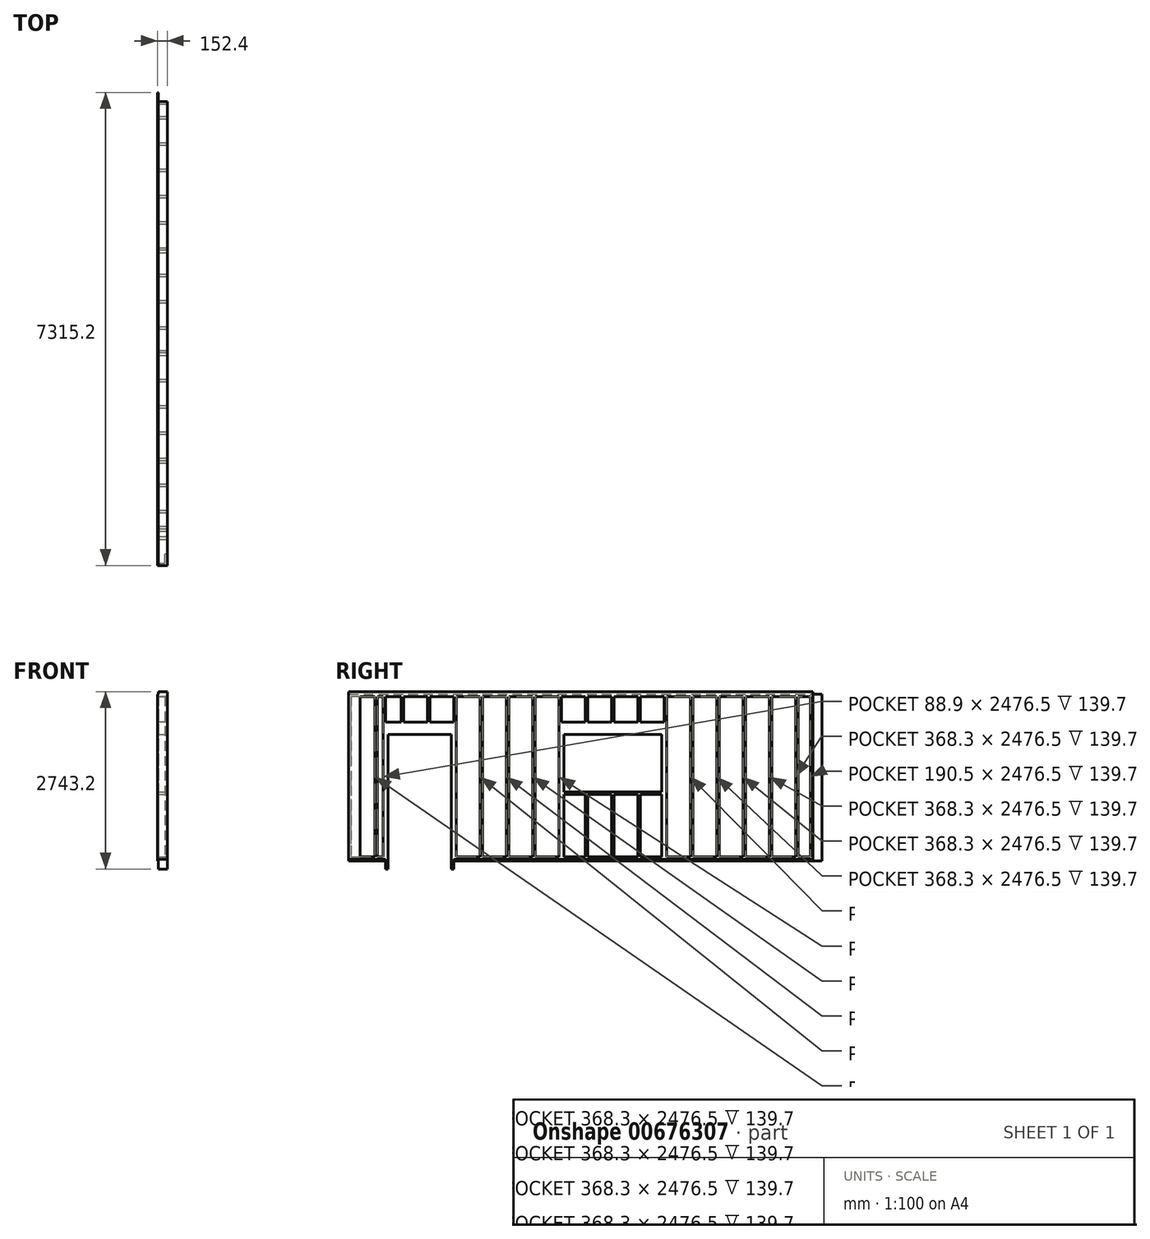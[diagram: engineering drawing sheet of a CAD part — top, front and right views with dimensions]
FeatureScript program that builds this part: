
annotation { "Feature Type Name" : "Feature", "Feature Type Description" : "" }
export const myFeature = defineFeature(function(context is Context, id is Id, definition is map)
    precondition{}
    {
        {
            var Q0;
            Q0=qCreatedBy(makeId("Top.planeOp"),FACE);
            var sketch = newSketch(context, id + "F0", { "sketchPlane" : qUnion([Q0])});
            skLineSegment(sketch, "E0.bottom", {"start": v(-69.85, 3587.75) * mm, "end": v(69.85, 3587.75) * mm});
            skLineSegment(sketch, "E0.top", {"start": v(-69.85, -3587.75) * mm, "end": v(69.85, -3587.75) * mm});
            skLineSegment(sketch, "E0.left", {"start": v(-69.85, 3587.75) * mm, "end": v(-69.85, -3587.75) * mm});
            skLineSegment(sketch, "E0.right", {"start": v(69.85, 3587.75) * mm, "end": v(69.85, -3587.75) * mm});
            skPoint(sketch, "E0.middle", {"position": v(0, 0) * mm});
            skSolve(sketch);
        }
        {
            var Q0;
            Q0 = qSketchRegion(id + "F0", true);
            extrude(context, id + "F1", {"entities" : qUnion([Q0]), "depth" : 38.1 * mm, "offsetDistance" : 25.4 * mm});
        }
        {
            var Q0;
            Q0=makeQuery(id+"F1.opExtrude","SWEPT_FACE",FACE,{"disambiguationData":[OSD([sQuery(id+"F0.wireOp",EDGE,"E0.right")])]});
            var sketch = newSketch(context, id + "F2", { "sketchPlane" : qUnion([Q0])});
            skLineSegment(sketch, "E1.bottom", {"start": v(-3587.75, 38.1) * mm, "end": v(3587.75, 38.1) * mm, "construction": true});
            skLineSegment(sketch, "E1.top", {"start": v(-3587.75, 2590.8) * mm, "end": v(3587.75, 2590.8) * mm});
            skLineSegment(sketch, "E1.left", {"start": v(-3587.75, 38.1) * mm, "end": v(-3587.75, 2590.8) * mm});
            skLineSegment(sketch, "E1.right", {"start": v(3587.75, 38.1) * mm, "end": v(3587.75, 2590.8) * mm});
            skLineSegment(sketch, "E2.0", {"start": v(3549.65, 38.1) * mm, "end": v(3549.65, 2514.6) * mm});
            skLineSegment(sketch, "E3.0", {"start": v(-3549.65, 38.1) * mm, "end": v(-3549.65, 2514.6) * mm});
            skLineSegment(sketch, "E4", {"start": v(3549.65, 38.1) * mm, "end": v(3587.75, 38.1) * mm});
            skLineSegment(sketch, "E5", {"start": v(-3549.65, 38.1) * mm, "end": v(-3587.75, 38.1) * mm});
            skLineSegment(sketch, "E6.trimOffspring", {"start": v(-3549.65, 2514.6) * mm, "end": v(3549.65, 2514.6) * mm});
            skSolve(sketch);
        }
        {
            var Q0;
            Q0 = qSketchRegion(id + "F2", true);
            var Q1;
            Q1=makeQuery(id+"F1.opExtrude","SWEPT_FACE",FACE,{"disambiguationData":[OSD([sQuery(id+"F0.wireOp",EDGE,"E0.left")])]});
            extrude(context, id + "F3", {"entities" : qUnion([Q0]), "operationType" : NewBodyOperationType.ADD, "endBound" : BoundingType.UP_TO_SURFACE, "oppositeDirection" : true, "depth" : 289.56 * mm, "endBoundEntityFace" : qUnion([Q1]), "offsetDistance" : 25.4 * mm});
        }
        {
            var Q0;
            Q0=makeQuery(id+"F1.opExtrude","CAP_FACE",FACE,{"disambiguationData":[OSD([sQuery(id+"F0.wireOp",EDGE,"E0.bottom"),sQuery(id+"F0.wireOp",EDGE,"E0.top"),sQuery(id+"F0.wireOp",EDGE,"E0.left"),sQuery(id+"F0.wireOp",EDGE,"E0.right")])],"isStart":false});
            var sketch = newSketch(context, id + "F4", { "sketchPlane" : qUnion([Q0])});
            skLineSegment(sketch, "E7.bottom", {"start": v(-69.85, -3181.35) * mm, "end": v(69.85, -3181.35) * mm});
            skLineSegment(sketch, "E7.top", {"start": v(-69.85, -3143.25) * mm, "end": v(69.85, -3143.25) * mm});
            skLineSegment(sketch, "E7.left", {"start": v(-69.85, -3181.35) * mm, "end": v(-69.85, -3143.25) * mm});
            skLineSegment(sketch, "E7.right", {"start": v(69.85, -3181.35) * mm, "end": v(69.85, -3143.25) * mm});
            skLineSegment(sketch, "E8.0.1.0", {"start": v(69.85, -2774.95) * mm, "end": v(69.85, -2736.85) * mm});
            skLineSegment(sketch, "E8.0.1.1", {"start": v(-69.85, -2736.85) * mm, "end": v(69.85, -2736.85) * mm});
            skLineSegment(sketch, "E8.0.1.2", {"start": v(-69.85, -2774.95) * mm, "end": v(69.85, -2774.95) * mm});
            skLineSegment(sketch, "E8.0.1.3", {"start": v(-69.85, -2774.95) * mm, "end": v(-69.85, -2736.85) * mm});
            skLineSegment(sketch, "E8.0.2.0", {"start": v(69.85, -2368.55) * mm, "end": v(69.85, -2330.45) * mm});
            skLineSegment(sketch, "E8.0.2.1", {"start": v(-69.85, -2330.45) * mm, "end": v(69.85, -2330.45) * mm});
            skLineSegment(sketch, "E8.0.2.2", {"start": v(-69.85, -2368.55) * mm, "end": v(69.85, -2368.55) * mm});
            skLineSegment(sketch, "E8.0.2.3", {"start": v(-69.85, -2368.55) * mm, "end": v(-69.85, -2330.45) * mm});
            skLineSegment(sketch, "E8.0.3.0", {"start": v(69.85, -1962.15) * mm, "end": v(69.85, -1924.05) * mm});
            skLineSegment(sketch, "E8.0.3.1", {"start": v(-69.85, -1924.05) * mm, "end": v(69.85, -1924.05) * mm});
            skLineSegment(sketch, "E8.0.3.2", {"start": v(-69.85, -1962.15) * mm, "end": v(69.85, -1962.15) * mm});
            skLineSegment(sketch, "E8.0.3.3", {"start": v(-69.85, -1962.15) * mm, "end": v(-69.85, -1924.05) * mm});
            skLineSegment(sketch, "E8.0.4.0", {"start": v(69.85, -1555.75) * mm, "end": v(69.85, -1517.65) * mm});
            skLineSegment(sketch, "E8.0.4.1", {"start": v(-69.85, -1517.65) * mm, "end": v(69.85, -1517.65) * mm});
            skLineSegment(sketch, "E8.0.4.2", {"start": v(-69.85, -1555.75) * mm, "end": v(69.85, -1555.75) * mm});
            skLineSegment(sketch, "E8.0.4.3", {"start": v(-69.85, -1555.75) * mm, "end": v(-69.85, -1517.65) * mm});
            skLineSegment(sketch, "E8.0.5.0", {"start": v(69.85, -1149.35) * mm, "end": v(69.85, -1111.25) * mm});
            skLineSegment(sketch, "E8.0.5.1", {"start": v(-69.85, -1111.25) * mm, "end": v(69.85, -1111.25) * mm});
            skLineSegment(sketch, "E8.0.5.2", {"start": v(-69.85, -1149.35) * mm, "end": v(69.85, -1149.35) * mm});
            skLineSegment(sketch, "E8.0.5.3", {"start": v(-69.85, -1149.35) * mm, "end": v(-69.85, -1111.25) * mm});
            skLineSegment(sketch, "E8.0.6.0", {"start": v(69.85, -742.95) * mm, "end": v(69.85, -704.85) * mm});
            skLineSegment(sketch, "E8.0.6.1", {"start": v(-69.85, -704.85) * mm, "end": v(69.85, -704.85) * mm});
            skLineSegment(sketch, "E8.0.6.2", {"start": v(-69.85, -742.95) * mm, "end": v(69.85, -742.95) * mm});
            skLineSegment(sketch, "E8.0.6.3", {"start": v(-69.85, -742.95) * mm, "end": v(-69.85, -704.85) * mm});
            skLineSegment(sketch, "E8.0.7.0", {"start": v(69.85, -336.55) * mm, "end": v(69.85, -298.45) * mm});
            skLineSegment(sketch, "E8.0.7.1", {"start": v(-69.85, -298.45) * mm, "end": v(69.85, -298.45) * mm});
            skLineSegment(sketch, "E8.0.7.2", {"start": v(-69.85, -336.55) * mm, "end": v(69.85, -336.55) * mm});
            skLineSegment(sketch, "E8.0.7.3", {"start": v(-69.85, -336.55) * mm, "end": v(-69.85, -298.45) * mm});
            skLineSegment(sketch, "E8.0.8.0", {"start": v(69.85, 69.85) * mm, "end": v(69.85, 107.95) * mm});
            skLineSegment(sketch, "E8.0.8.1", {"start": v(-69.85, 107.95) * mm, "end": v(69.85, 107.95) * mm});
            skLineSegment(sketch, "E8.0.8.2", {"start": v(-69.85, 69.85) * mm, "end": v(69.85, 69.85) * mm});
            skLineSegment(sketch, "E8.0.8.3", {"start": v(-69.85, 69.85) * mm, "end": v(-69.85, 107.95) * mm});
            skLineSegment(sketch, "E8.0.9.0", {"start": v(69.85, 476.25) * mm, "end": v(69.85, 514.35) * mm});
            skLineSegment(sketch, "E8.0.9.1", {"start": v(-69.85, 514.35) * mm, "end": v(69.85, 514.35) * mm});
            skLineSegment(sketch, "E8.0.9.2", {"start": v(-69.85, 476.25) * mm, "end": v(69.85, 476.25) * mm});
            skLineSegment(sketch, "E8.0.9.3", {"start": v(-69.85, 476.25) * mm, "end": v(-69.85, 514.35) * mm});
            skLineSegment(sketch, "E8.0.10.0", {"start": v(69.85, 882.65) * mm, "end": v(69.85, 920.75) * mm});
            skLineSegment(sketch, "E8.0.10.1", {"start": v(-69.85, 920.75) * mm, "end": v(69.85, 920.75) * mm});
            skLineSegment(sketch, "E8.0.10.2", {"start": v(-69.85, 882.65) * mm, "end": v(69.85, 882.65) * mm});
            skLineSegment(sketch, "E8.0.10.3", {"start": v(-69.85, 882.65) * mm, "end": v(-69.85, 920.75) * mm});
            skLineSegment(sketch, "E8.0.11.0", {"start": v(69.85, 1289.05) * mm, "end": v(69.85, 1327.15) * mm});
            skLineSegment(sketch, "E8.0.11.1", {"start": v(-69.85, 1327.15) * mm, "end": v(69.85, 1327.15) * mm});
            skLineSegment(sketch, "E8.0.11.2", {"start": v(-69.85, 1289.05) * mm, "end": v(69.85, 1289.05) * mm});
            skLineSegment(sketch, "E8.0.11.3", {"start": v(-69.85, 1289.05) * mm, "end": v(-69.85, 1327.15) * mm});
            skLineSegment(sketch, "E8.0.12.0", {"start": v(69.85, 1695.45) * mm, "end": v(69.85, 1733.55) * mm});
            skLineSegment(sketch, "E8.0.12.1", {"start": v(-69.85, 1733.55) * mm, "end": v(69.85, 1733.55) * mm});
            skLineSegment(sketch, "E8.0.12.2", {"start": v(-69.85, 1695.45) * mm, "end": v(69.85, 1695.45) * mm});
            skLineSegment(sketch, "E8.0.12.3", {"start": v(-69.85, 1695.45) * mm, "end": v(-69.85, 1733.55) * mm});
            skLineSegment(sketch, "E8.0.13.0", {"start": v(69.85, 2101.85) * mm, "end": v(69.85, 2139.95) * mm});
            skLineSegment(sketch, "E8.0.13.1", {"start": v(-69.85, 2139.95) * mm, "end": v(69.85, 2139.95) * mm});
            skLineSegment(sketch, "E8.0.13.2", {"start": v(-69.85, 2101.85) * mm, "end": v(69.85, 2101.85) * mm});
            skLineSegment(sketch, "E8.0.13.3", {"start": v(-69.85, 2101.85) * mm, "end": v(-69.85, 2139.95) * mm});
            skLineSegment(sketch, "E8.0.14.0", {"start": v(69.85, 2508.25) * mm, "end": v(69.85, 2546.35) * mm});
            skLineSegment(sketch, "E8.0.14.1", {"start": v(-69.85, 2546.35) * mm, "end": v(69.85, 2546.35) * mm});
            skLineSegment(sketch, "E8.0.14.2", {"start": v(-69.85, 2508.25) * mm, "end": v(69.85, 2508.25) * mm});
            skLineSegment(sketch, "E8.0.14.3", {"start": v(-69.85, 2508.25) * mm, "end": v(-69.85, 2546.35) * mm});
            skLineSegment(sketch, "E8.0.15.0", {"start": v(69.85, 2914.65) * mm, "end": v(69.85, 2952.75) * mm});
            skLineSegment(sketch, "E8.0.15.1", {"start": v(-69.85, 2952.75) * mm, "end": v(69.85, 2952.75) * mm});
            skLineSegment(sketch, "E8.0.15.2", {"start": v(-69.85, 2914.65) * mm, "end": v(69.85, 2914.65) * mm});
            skLineSegment(sketch, "E8.0.15.3", {"start": v(-69.85, 2914.65) * mm, "end": v(-69.85, 2952.75) * mm});
            skLineSegment(sketch, "E8.0.16.0", {"start": v(69.85, 3321.05) * mm, "end": v(69.85, 3359.15) * mm});
            skLineSegment(sketch, "E8.0.16.1", {"start": v(-69.85, 3359.15) * mm, "end": v(69.85, 3359.15) * mm});
            skLineSegment(sketch, "E8.0.16.2", {"start": v(-69.85, 3321.05) * mm, "end": v(69.85, 3321.05) * mm});
            skLineSegment(sketch, "E8.0.16.3", {"start": v(-69.85, 3321.05) * mm, "end": v(-69.85, 3359.15) * mm});
            skLineSegment(sketch, "E8.direction1", {"start": v(-69.85, -3181.35) * mm, "end": v(-44.45, -3181.35) * mm, "construction": true});
            skLineSegment(sketch, "E8.direction2", {"start": v(-69.85, -3181.35) * mm, "end": v(-69.85, -2774.95) * mm, "construction": true});
            skLineSegment(sketch, "E9.bottom", {"start": v(69.85, -3549.65) * mm, "end": v(31.75, -3549.65) * mm});
            skLineSegment(sketch, "E9.top", {"start": v(69.85, -3409.95) * mm, "end": v(31.75, -3409.95) * mm});
            skLineSegment(sketch, "E9.left", {"start": v(69.85, -3549.65) * mm, "end": v(69.85, -3409.95) * mm});
            skLineSegment(sketch, "E9.right", {"start": v(31.75, -3549.65) * mm, "end": v(31.75, -3409.95) * mm});
            skSolve(sketch);
        }
        {
            var Q0;
            Q0 = qSketchRegion(id + "F4", true);
            var Q1;
            Q1=makeQuery(id+"F3.opExtrude","SWEPT_FACE",FACE,{"disambiguationData":[OSD([sQuery(id+"F2.wireOp",EDGE,"E6.trimOffspring")])]});
            extrude(context, id + "F5", {"entities" : qUnion([Q0]), "operationType" : NewBodyOperationType.ADD, "endBound" : BoundingType.UP_TO_SURFACE, "depth" : 25.4 * mm, "endBoundEntityFace" : qUnion([Q1]), "offsetDistance" : 25.4 * mm});
        }
        {
            var Q0;
            Q0=makeQuery(id+"F5.boolean.opBoolean","MERGE",FACE,{"derivedFrom":[makeQuery(id+"F3.boolean.opBoolean","MERGE",FACE,{"derivedFrom":[makeQuery(id+"F1.opExtrude","SWEPT_FACE",FACE,{"disambiguationData":[OSD([sQuery(id+"F0.wireOp",EDGE,"E0.right")])]}),makeQuery(id+"F3.opExtrude","CAP_FACE",FACE,{"disambiguationData":[OSD([sQuery(id+"F2.wireOp",EDGE,"E1.top"),sQuery(id+"F2.wireOp",EDGE,"E1.left"),sQuery(id+"F2.wireOp",EDGE,"E1.right"),sQuery(id+"F2.wireOp",EDGE,"E2.0"),sQuery(id+"F2.wireOp",EDGE,"E3.0"),sQuery(id+"F2.wireOp",EDGE,"E4"),sQuery(id+"F2.wireOp",EDGE,"E5"),sQuery(id+"F2.wireOp",EDGE,"E6.trimOffspring")])],"isStart":true})]}),makeQuery(id+"F5.opExtrude","SWEPT_FACE",FACE,{"disambiguationData":[OSD([sQuery(id+"F4.wireOp",EDGE,"E7.right")])]}),makeQuery(id+"F5.opExtrude","SWEPT_FACE",FACE,{"disambiguationData":[OSD([sQuery(id+"F4.wireOp",EDGE,"E8.0.1.0")])]}),makeQuery(id+"F5.opExtrude","SWEPT_FACE",FACE,{"disambiguationData":[OSD([sQuery(id+"F4.wireOp",EDGE,"E8.0.2.0")])]}),makeQuery(id+"F5.opExtrude","SWEPT_FACE",FACE,{"disambiguationData":[OSD([sQuery(id+"F4.wireOp",EDGE,"E8.0.3.0")])]}),makeQuery(id+"F5.opExtrude","SWEPT_FACE",FACE,{"disambiguationData":[OSD([sQuery(id+"F4.wireOp",EDGE,"E8.0.4.0")])]}),makeQuery(id+"F5.opExtrude","SWEPT_FACE",FACE,{"disambiguationData":[OSD([sQuery(id+"F4.wireOp",EDGE,"E8.0.5.0")])]}),makeQuery(id+"F5.opExtrude","SWEPT_FACE",FACE,{"disambiguationData":[OSD([sQuery(id+"F4.wireOp",EDGE,"E8.0.6.0")])]}),makeQuery(id+"F5.opExtrude","SWEPT_FACE",FACE,{"disambiguationData":[OSD([sQuery(id+"F4.wireOp",EDGE,"E8.0.7.0")])]}),makeQuery(id+"F5.opExtrude","SWEPT_FACE",FACE,{"disambiguationData":[OSD([sQuery(id+"F4.wireOp",EDGE,"E8.0.8.0")])]}),makeQuery(id+"F5.opExtrude","SWEPT_FACE",FACE,{"disambiguationData":[OSD([sQuery(id+"F4.wireOp",EDGE,"E8.0.9.0")])]}),makeQuery(id+"F5.opExtrude","SWEPT_FACE",FACE,{"disambiguationData":[OSD([sQuery(id+"F4.wireOp",EDGE,"E8.0.10.0")])]}),makeQuery(id+"F5.opExtrude","SWEPT_FACE",FACE,{"disambiguationData":[OSD([sQuery(id+"F4.wireOp",EDGE,"E8.0.11.0")])]}),makeQuery(id+"F5.opExtrude","SWEPT_FACE",FACE,{"disambiguationData":[OSD([sQuery(id+"F4.wireOp",EDGE,"E8.0.12.0")])]}),makeQuery(id+"F5.opExtrude","SWEPT_FACE",FACE,{"disambiguationData":[OSD([sQuery(id+"F4.wireOp",EDGE,"E8.0.13.0")])]}),makeQuery(id+"F5.opExtrude","SWEPT_FACE",FACE,{"disambiguationData":[OSD([sQuery(id+"F4.wireOp",EDGE,"E8.0.14.0")])]}),makeQuery(id+"F5.opExtrude","SWEPT_FACE",FACE,{"disambiguationData":[OSD([sQuery(id+"F4.wireOp",EDGE,"E8.0.15.0")])]}),makeQuery(id+"F5.opExtrude","SWEPT_FACE",FACE,{"disambiguationData":[OSD([sQuery(id+"F4.wireOp",EDGE,"E8.0.16.0")])]})]});
            var sketch = newSketch(context, id + "F6", { "sketchPlane" : qUnion([Q0])});
            skLineSegment(sketch, "E10", {"start": v(-3054.35, 38.1) * mm, "end": v(-3054.35, 2514.6) * mm});
            skLineSegment(sketch, "E11", {"start": v(-3054.35, 2514.6) * mm, "end": v(-3016.25, 2514.6) * mm});
            skLineSegment(sketch, "E12", {"start": v(-3016.25, 2514.6) * mm, "end": v(-3016.25, 2120.9) * mm});
            skLineSegment(sketch, "E13", {"start": v(-3016.25, 2120.9) * mm, "end": v(-1962.15, 2120.9) * mm});
            skLineSegment(sketch, "E14", {"start": v(-2000.25, 38.1) * mm, "end": v(-2000.25, 1930.4) * mm});
            skLineSegment(sketch, "E15", {"start": v(-2000.25, 1930.4) * mm, "end": v(-2978.15, 1930.4) * mm});
            skLineSegment(sketch, "E16", {"start": v(-2978.15, 1930.4) * mm, "end": v(-2978.15, 38.1) * mm});
            skLineSegment(sketch, "E17", {"start": v(-2978.15, 38.1) * mm, "end": v(-3054.35, 38.1) * mm});
            skLineSegment(sketch, "E18", {"start": v(-1962.15, 2120.9) * mm, "end": v(-1962.15, 38.1) * mm});
            skLineSegment(sketch, "E19", {"start": v(-1962.15, 38.1) * mm, "end": v(-2000.25, 38.1) * mm});
            skLineSegment(sketch, "E20.bottom", {"start": v(-260.35, 1930.4) * mm, "end": v(1250.95, 1930.4) * mm});
            skLineSegment(sketch, "E20.top", {"start": v(-260.35, 1041.4) * mm, "end": v(1250.95, 1041.4) * mm});
            skLineSegment(sketch, "E20.left", {"start": v(-260.35, 1930.4) * mm, "end": v(-260.35, 1041.4) * mm});
            skLineSegment(sketch, "E20.right", {"start": v(1250.95, 1930.4) * mm, "end": v(1250.95, 1041.4) * mm});
            skLineSegment(sketch, "E21", {"start": v(-260.35, 1003.3) * mm, "end": v(-260.35, 38.1) * mm});
            skLineSegment(sketch, "E22", {"start": v(-260.35, 38.1) * mm, "end": v(-298.45, 38.1) * mm});
            skLineSegment(sketch, "E23", {"start": v(-298.45, 38.1) * mm, "end": v(-298.45, 2120.9) * mm});
            skLineSegment(sketch, "E24", {"start": v(-298.45, 2120.9) * mm, "end": v(1289.05, 2120.9) * mm});
            skLineSegment(sketch, "E25", {"start": v(1289.05, 2120.9) * mm, "end": v(1289.05, 38.1) * mm});
            skLineSegment(sketch, "E26", {"start": v(1289.05, 38.1) * mm, "end": v(1250.95, 38.1) * mm});
            skLineSegment(sketch, "E27", {"start": v(1250.95, 38.1) * mm, "end": v(1250.95, 1003.3) * mm});
            skLineSegment(sketch, "E28", {"start": v(1250.95, 1003.3) * mm, "end": v(-260.35, 1003.3) * mm});
            skLineSegment(sketch, "E29.bottom", {"start": v(-3016.25, 0) * mm, "end": v(-2978.15, 0) * mm});
            skLineSegment(sketch, "E29.top", {"start": v(-3016.25, -152.4) * mm, "end": v(-2978.15, -152.4) * mm});
            skLineSegment(sketch, "E29.left", {"start": v(-3016.25, 0) * mm, "end": v(-3016.25, -152.4) * mm});
            skLineSegment(sketch, "E29.right", {"start": v(-2978.15, 0) * mm, "end": v(-2978.15, -152.4) * mm});
            skLineSegment(sketch, "E30.bottom", {"start": v(-1962.15, 0) * mm, "end": v(-2000.25, 0) * mm});
            skLineSegment(sketch, "E30.top", {"start": v(-1962.15, -152.4) * mm, "end": v(-2000.25, -152.4) * mm});
            skLineSegment(sketch, "E30.left", {"start": v(-1962.15, 0) * mm, "end": v(-1962.15, -152.4) * mm});
            skLineSegment(sketch, "E30.right", {"start": v(-2000.25, 0) * mm, "end": v(-2000.25, -152.4) * mm});
            skSolve(sketch);
        }
        {
            var Q0;
            Q0 = qSketchRegion(id + "F6", true);
            extrude(context, id + "F7", {"entities" : qUnion([Q0]), "operationType" : NewBodyOperationType.ADD, "oppositeDirection" : true, "depth" : 139.7 * mm, "offsetDistance" : 25.4 * mm});
        }
        {
            var Q0;
            {var subQ0=sQuery(id+"F0.wireOp",EDGE,"E0.left");Q0=makeQuery(id+"F7.boolean.opBoolean","MERGE",FACE,{"derivedFrom":[makeQuery(id+"F5.boolean.opBoolean","MERGE",FACE,{"derivedFrom":[makeQuery(id+"F3.boolean.opBoolean","MERGE",FACE,{"derivedFrom":[makeQuery(id+"F1.opExtrude","SWEPT_FACE",FACE,{"disambiguationData":[OSD([subQ0])]}),makeQuery(id+"F3.opExtrude","CAP_FACE",FACE,{"disambiguationData":[OSD([subQ0])],"isStart":false})]}),makeQuery(id+"F5.opExtrude","SWEPT_FACE",FACE,{"disambiguationData":[OSD([sQuery(id+"F4.wireOp",EDGE,"E7.left")])]}),makeQuery(id+"F5.opExtrude","SWEPT_FACE",FACE,{"disambiguationData":[OSD([sQuery(id+"F4.wireOp",EDGE,"E8.0.1.3")])]}),makeQuery(id+"F5.opExtrude","SWEPT_FACE",FACE,{"disambiguationData":[OSD([sQuery(id+"F4.wireOp",EDGE,"E8.0.2.3")])]}),makeQuery(id+"F5.opExtrude","SWEPT_FACE",FACE,{"disambiguationData":[OSD([sQuery(id+"F4.wireOp",EDGE,"E8.0.3.3")])]}),makeQuery(id+"F5.opExtrude","SWEPT_FACE",FACE,{"disambiguationData":[OSD([sQuery(id+"F4.wireOp",EDGE,"E8.0.4.3")])]}),makeQuery(id+"F5.opExtrude","SWEPT_FACE",FACE,{"disambiguationData":[OSD([sQuery(id+"F4.wireOp",EDGE,"E8.0.5.3")])]}),makeQuery(id+"F5.opExtrude","SWEPT_FACE",FACE,{"disambiguationData":[OSD([sQuery(id+"F4.wireOp",EDGE,"E8.0.6.3")])]}),makeQuery(id+"F5.opExtrude","SWEPT_FACE",FACE,{"disambiguationData":[OSD([sQuery(id+"F4.wireOp",EDGE,"E8.0.7.3")])]}),makeQuery(id+"F5.opExtrude","SWEPT_FACE",FACE,{"disambiguationData":[OSD([sQuery(id+"F4.wireOp",EDGE,"E8.0.8.3")])]}),makeQuery(id+"F5.opExtrude","SWEPT_FACE",FACE,{"disambiguationData":[OSD([sQuery(id+"F4.wireOp",EDGE,"E8.0.9.3")])]}),makeQuery(id+"F5.opExtrude","SWEPT_FACE",FACE,{"disambiguationData":[OSD([sQuery(id+"F4.wireOp",EDGE,"E8.0.10.3")])]}),makeQuery(id+"F5.opExtrude","SWEPT_FACE",FACE,{"disambiguationData":[OSD([sQuery(id+"F4.wireOp",EDGE,"E8.0.11.3")])]}),makeQuery(id+"F5.opExtrude","SWEPT_FACE",FACE,{"disambiguationData":[OSD([sQuery(id+"F4.wireOp",EDGE,"E8.0.12.3")])]}),makeQuery(id+"F5.opExtrude","SWEPT_FACE",FACE,{"disambiguationData":[OSD([sQuery(id+"F4.wireOp",EDGE,"E8.0.13.3")])]}),makeQuery(id+"F5.opExtrude","SWEPT_FACE",FACE,{"disambiguationData":[OSD([sQuery(id+"F4.wireOp",EDGE,"E8.0.14.3")])]}),makeQuery(id+"F5.opExtrude","SWEPT_FACE",FACE,{"disambiguationData":[OSD([sQuery(id+"F4.wireOp",EDGE,"E8.0.15.3")])]}),makeQuery(id+"F5.opExtrude","SWEPT_FACE",FACE,{"disambiguationData":[OSD([sQuery(id+"F4.wireOp",EDGE,"E8.0.16.3")])]})]}),makeQuery(id+"F7.opExtrude","CAP_FACE",FACE,{"disambiguationData":[OSD([sQuery(id+"F6.wireOp",EDGE,"E10"),sQuery(id+"F6.wireOp",EDGE,"E11"),sQuery(id+"F6.wireOp",EDGE,"E12"),sQuery(id+"F6.wireOp",EDGE,"E13"),sQuery(id+"F6.wireOp",EDGE,"E14"),sQuery(id+"F6.wireOp",EDGE,"E15"),sQuery(id+"F6.wireOp",EDGE,"E16"),sQuery(id+"F6.wireOp",EDGE,"E17"),sQuery(id+"F6.wireOp",EDGE,"E18"),sQuery(id+"F6.wireOp",EDGE,"E19")])],"isStart":false}),makeQuery(id+"F7.opExtrude","CAP_FACE",FACE,{"disambiguationData":[OSD([sQuery(id+"F6.wireOp",EDGE,"E20.bottom"),sQuery(id+"F6.wireOp",EDGE,"E20.top"),sQuery(id+"F6.wireOp",EDGE,"E20.left"),sQuery(id+"F6.wireOp",EDGE,"E20.right"),sQuery(id+"F6.wireOp",EDGE,"E21"),sQuery(id+"F6.wireOp",EDGE,"E22"),sQuery(id+"F6.wireOp",EDGE,"E23"),sQuery(id+"F6.wireOp",EDGE,"E24"),sQuery(id+"F6.wireOp",EDGE,"E25"),sQuery(id+"F6.wireOp",EDGE,"E26"),sQuery(id+"F6.wireOp",EDGE,"E27"),sQuery(id+"F6.wireOp",EDGE,"E28")])],"isStart":false}),makeQuery(id+"F7.opExtrude","CAP_FACE",FACE,{"disambiguationData":[OSD([sQuery(id+"F6.wireOp",EDGE,"E29.bottom"),sQuery(id+"F6.wireOp",EDGE,"E29.top"),sQuery(id+"F6.wireOp",EDGE,"E29.left"),sQuery(id+"F6.wireOp",EDGE,"E29.right")])],"isStart":false}),makeQuery(id+"F7.opExtrude","CAP_FACE",FACE,{"disambiguationData":[OSD([sQuery(id+"F6.wireOp",EDGE,"E30.bottom"),sQuery(id+"F6.wireOp",EDGE,"E30.top"),sQuery(id+"F6.wireOp",EDGE,"E30.left"),sQuery(id+"F6.wireOp",EDGE,"E30.right")])],"isStart":false})]});}
            var sketch = newSketch(context, id + "F8", { "sketchPlane" : qUnion([Q0])});
            skLineSegment(sketch, "E31.bottom", {"start": v(3587.75, 2552.7) * mm, "end": v(-3727.45, 2552.7) * mm});
            skLineSegment(sketch, "E31.top", {"start": v(3587.75, -25.4) * mm, "end": v(-3727.45, -25.4) * mm});
            skLineSegment(sketch, "E31.left", {"start": v(3587.75, 2552.7) * mm, "end": v(3587.75, -25.4) * mm});
            skLineSegment(sketch, "E31.right", {"start": v(-3727.45, 2552.7) * mm, "end": v(-3727.45, -25.4) * mm});
            skSolve(sketch);
        }
        {
            var Q0;
            Q0 = qSketchRegion(id + "F8", true);
            extrude(context, id + "F9", {"entities" : qUnion([Q0]), "operationType" : NewBodyOperationType.ADD, "depth" : 12.7 * mm, "offsetDistance" : 25.4 * mm});
        }
        {
            var Q0;
            Q0=makeQuery(id+"F7.boolean.opBoolean","MERGE",FACE,{"derivedFrom":[makeQuery(id+"F5.boolean.opBoolean","MERGE",FACE,{"derivedFrom":[makeQuery(id+"F3.boolean.opBoolean","MERGE",FACE,{"derivedFrom":[makeQuery(id+"F1.opExtrude","SWEPT_FACE",FACE,{"disambiguationData":[OSD([sQuery(id+"F0.wireOp",EDGE,"E0.right")])]}),makeQuery(id+"F3.opExtrude","CAP_FACE",FACE,{"disambiguationData":[OSD([sQuery(id+"F2.wireOp",EDGE,"E1.top"),sQuery(id+"F2.wireOp",EDGE,"E1.left"),sQuery(id+"F2.wireOp",EDGE,"E1.right"),sQuery(id+"F2.wireOp",EDGE,"E2.0"),sQuery(id+"F2.wireOp",EDGE,"E3.0"),sQuery(id+"F2.wireOp",EDGE,"E4"),sQuery(id+"F2.wireOp",EDGE,"E5"),sQuery(id+"F2.wireOp",EDGE,"E6.trimOffspring")])],"isStart":true})]}),makeQuery(id+"F5.opExtrude","SWEPT_FACE",FACE,{"disambiguationData":[OSD([sQuery(id+"F4.wireOp",EDGE,"E7.right")])]}),makeQuery(id+"F5.opExtrude","SWEPT_FACE",FACE,{"disambiguationData":[OSD([sQuery(id+"F4.wireOp",EDGE,"E8.0.1.0")])]}),makeQuery(id+"F5.opExtrude","SWEPT_FACE",FACE,{"disambiguationData":[OSD([sQuery(id+"F4.wireOp",EDGE,"E8.0.2.0")])]}),makeQuery(id+"F5.opExtrude","SWEPT_FACE",FACE,{"disambiguationData":[OSD([sQuery(id+"F4.wireOp",EDGE,"E8.0.3.0")])]}),makeQuery(id+"F5.opExtrude","SWEPT_FACE",FACE,{"disambiguationData":[OSD([sQuery(id+"F4.wireOp",EDGE,"E8.0.4.0")])]}),makeQuery(id+"F5.opExtrude","SWEPT_FACE",FACE,{"disambiguationData":[OSD([sQuery(id+"F4.wireOp",EDGE,"E8.0.5.0")])]}),makeQuery(id+"F5.opExtrude","SWEPT_FACE",FACE,{"disambiguationData":[OSD([sQuery(id+"F4.wireOp",EDGE,"E8.0.6.0")])]}),makeQuery(id+"F5.opExtrude","SWEPT_FACE",FACE,{"disambiguationData":[OSD([sQuery(id+"F4.wireOp",EDGE,"E8.0.7.0")])]}),makeQuery(id+"F5.opExtrude","SWEPT_FACE",FACE,{"disambiguationData":[OSD([sQuery(id+"F4.wireOp",EDGE,"E8.0.8.0")])]}),makeQuery(id+"F5.opExtrude","SWEPT_FACE",FACE,{"disambiguationData":[OSD([sQuery(id+"F4.wireOp",EDGE,"E8.0.9.0")])]}),makeQuery(id+"F5.opExtrude","SWEPT_FACE",FACE,{"disambiguationData":[OSD([sQuery(id+"F4.wireOp",EDGE,"E8.0.10.0")])]}),makeQuery(id+"F5.opExtrude","SWEPT_FACE",FACE,{"disambiguationData":[OSD([sQuery(id+"F4.wireOp",EDGE,"E8.0.11.0")])]}),makeQuery(id+"F5.opExtrude","SWEPT_FACE",FACE,{"disambiguationData":[OSD([sQuery(id+"F4.wireOp",EDGE,"E8.0.12.0")])]}),makeQuery(id+"F5.opExtrude","SWEPT_FACE",FACE,{"disambiguationData":[OSD([sQuery(id+"F4.wireOp",EDGE,"E8.0.13.0")])]}),makeQuery(id+"F5.opExtrude","SWEPT_FACE",FACE,{"disambiguationData":[OSD([sQuery(id+"F4.wireOp",EDGE,"E8.0.14.0")])]}),makeQuery(id+"F5.opExtrude","SWEPT_FACE",FACE,{"disambiguationData":[OSD([sQuery(id+"F4.wireOp",EDGE,"E8.0.15.0")])]}),makeQuery(id+"F5.opExtrude","SWEPT_FACE",FACE,{"disambiguationData":[OSD([sQuery(id+"F4.wireOp",EDGE,"E8.0.16.0")])]})]}),makeQuery(id+"F7.opExtrude","CAP_FACE",FACE,{"disambiguationData":[OSD([sQuery(id+"F6.wireOp",EDGE,"E10"),sQuery(id+"F6.wireOp",EDGE,"E11"),sQuery(id+"F6.wireOp",EDGE,"E12"),sQuery(id+"F6.wireOp",EDGE,"E13"),sQuery(id+"F6.wireOp",EDGE,"E14"),sQuery(id+"F6.wireOp",EDGE,"E15"),sQuery(id+"F6.wireOp",EDGE,"E16"),sQuery(id+"F6.wireOp",EDGE,"E17"),sQuery(id+"F6.wireOp",EDGE,"E18"),sQuery(id+"F6.wireOp",EDGE,"E19")])],"isStart":true})]});
            var sketch = newSketch(context, id + "F10", { "sketchPlane" : qUnion([Q0])});
            skLineSegment(sketch, "E32.bottom", {"start": v(-260.35, 1930.4) * mm, "end": v(1250.95, 1930.4) * mm});
            skLineSegment(sketch, "E32.top", {"start": v(-260.35, 1041.4) * mm, "end": v(1250.95, 1041.4) * mm});
            skLineSegment(sketch, "E32.left", {"start": v(-260.35, 1930.4) * mm, "end": v(-260.35, 1041.4) * mm});
            skLineSegment(sketch, "E32.right", {"start": v(1250.95, 1930.4) * mm, "end": v(1250.95, 1041.4) * mm});
            skLineSegment(sketch, "E33.bottom", {"start": v(-2978.15, 1930.4) * mm, "end": v(-2000.25, 1930.4) * mm});
            skLineSegment(sketch, "E33.top", {"start": v(-2978.15, -152.4) * mm, "end": v(-2000.25, -152.4) * mm});
            skLineSegment(sketch, "E33.left", {"start": v(-2978.15, 1930.4) * mm, "end": v(-2978.15, -152.4) * mm});
            skLineSegment(sketch, "E33.right", {"start": v(-2000.25, 1930.4) * mm, "end": v(-2000.25, -152.4) * mm});
            skSolve(sketch);
        }
        {
            var Q0;
            Q0 = qSketchRegion(id + "F10", true);
            extrude(context, id + "F11", {"entities" : qUnion([Q0]), "operationType" : NewBodyOperationType.REMOVE, "endBound" : BoundingType.THROUGH_ALL, "oppositeDirection" : true, "depth" : 25.4 * mm, "offsetDistance" : 25.4 * mm});
        }
    });
